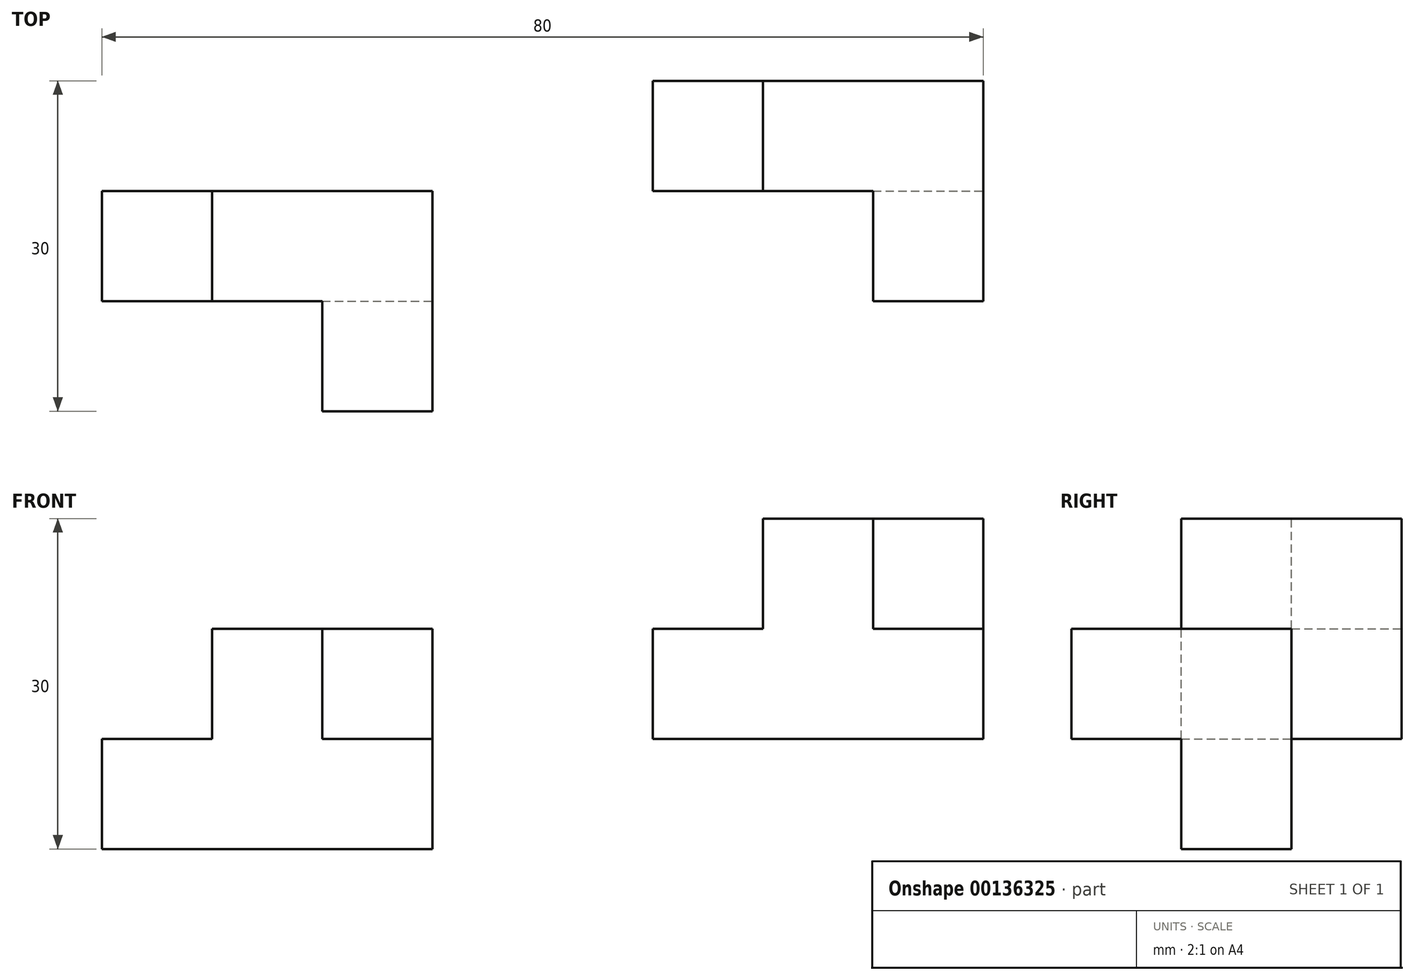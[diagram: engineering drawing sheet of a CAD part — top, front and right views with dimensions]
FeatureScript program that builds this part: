
annotation { "Feature Type Name" : "Feature", "Feature Type Description" : "" }
export const myFeature = defineFeature(function(context is Context, id is Id, definition is map)
    precondition{}
    {
        {
            var Q0;
            Q0=qCreatedBy(makeId("Front.planeOp"),FACE);
            var sketch = newSketch(context, id + "F0", { "sketchPlane" : qUnion([Q0])});
            skLineSegment(sketch, "E0.bottom", {"start": v(0, 0) * mm, "end": v(30, 0) * mm});
            skLineSegment(sketch, "E0.top", {"start": v(0, 20) * mm, "end": v(30, 20) * mm});
            skLineSegment(sketch, "E0.left", {"start": v(0, 0) * mm, "end": v(0, 20) * mm});
            skLineSegment(sketch, "E0.right", {"start": v(30, 0) * mm, "end": v(30, 20) * mm});
            skLineSegment(sketch, "E1.bottom", {"start": v(0, 20) * mm, "end": v(10, 20) * mm});
            skLineSegment(sketch, "E1.top", {"start": v(0, 10) * mm, "end": v(10, 10) * mm});
            skLineSegment(sketch, "E1.left", {"start": v(0, 20) * mm, "end": v(0, 10) * mm});
            skLineSegment(sketch, "E1.right", {"start": v(10, 20) * mm, "end": v(10, 10) * mm});
            skSolve(sketch);
        }
        {
            var Q0;
            Q0=makeQuery(id+"F0.imprint","IMPRINT",FACE,{"disambiguationData":[TD([[makeQuery(id+"F0.imprint","IMPRINT",EDGE,{"derivedFrom":sQuery(id+"F0.wireOp",EDGE,"E0.bottom")}),1.0]])]});
            extrude(context, id + "F1", {"entities" : qUnion([Q0]), "depth" : 10 * mm});
        }
        {
            var Q0;
            Q0=makeQuery(id+"F1.opExtrude","CAP_FACE",FACE,{"disambiguationData":[OSD([sQuery(id+"F0.wireOp",EDGE,"E0.bottom"),sQuery(id+"F0.wireOp",EDGE,"E0.top"),sQuery(id+"F0.wireOp",EDGE,"E0.left"),sQuery(id+"F0.wireOp",EDGE,"E0.right"),sQuery(id+"F0.wireOp",EDGE,"E1.top"),sQuery(id+"F0.wireOp",EDGE,"E1.right")])],"isStart":false});
            var sketch = newSketch(context, id + "F2", { "sketchPlane" : qUnion([Q0])});
            skLineSegment(sketch, "E2.bottom", {"start": v(30, 0) * mm, "end": v(20, 0) * mm});
            skLineSegment(sketch, "E2.top", {"start": v(30, 20) * mm, "end": v(20, 20) * mm});
            skLineSegment(sketch, "E2.left", {"start": v(30, 0) * mm, "end": v(30, 20) * mm});
            skLineSegment(sketch, "E2.right", {"start": v(20, 0) * mm, "end": v(20, 20) * mm});
            skLineSegment(sketch, "E3.bottom", {"start": v(20, 0) * mm, "end": v(30, 0) * mm});
            skLineSegment(sketch, "E3.top", {"start": v(20, 10) * mm, "end": v(30, 10) * mm});
            skLineSegment(sketch, "E3.left", {"start": v(20, 0) * mm, "end": v(20, 10) * mm});
            skLineSegment(sketch, "E3.right", {"start": v(30, 0) * mm, "end": v(30, 10) * mm});
            skSolve(sketch);
        }
        {
            var Q0;
            Q0=makeQuery(id+"F2.imprint","IMPRINT",FACE,{"disambiguationData":[TD([[makeQuery(id+"F2.imprint","IMPRINT",EDGE,{"derivedFrom":sQuery(id+"F2.wireOp",EDGE,"E2.top")}),-1.0]])]});
            extrude(context, id + "F3", {"entities" : qUnion([Q0]), "operationType" : NewBodyOperationType.ADD, "depth" : 10 * mm});
        }
        {
            var Q0;
            Q0=makeQuery(id+"F1.opExtrude","SWEPT_BODY",BODY,{"disambiguationData":[OSD([sQuery(id+"F0.wireOp",EDGE,"E0.bottom"),sQuery(id+"F0.wireOp",EDGE,"E0.top"),sQuery(id+"F0.wireOp",EDGE,"E0.left"),sQuery(id+"F0.wireOp",EDGE,"E0.right"),sQuery(id+"F0.wireOp",EDGE,"E1.top"),sQuery(id+"F0.wireOp",EDGE,"E1.right")])]});
            transform(context, id + "F4", {"entities" : qUnion([Q0]), "transformType" : TransformType.TRANSLATION_3D, "dx" : 50 * mm, "dy" : 10 * mm, "dz" : 10 * mm, "makeCopy" : true});
        }
    });
